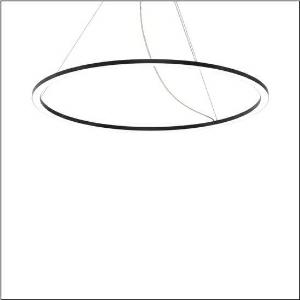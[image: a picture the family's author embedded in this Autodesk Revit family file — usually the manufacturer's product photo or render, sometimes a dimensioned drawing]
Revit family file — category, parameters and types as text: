
# Revit family: silica_r__21_ring-d_5pjbd4d1104a_1e9f
name_source: partatom
category: Lighting Fixtures
units: mm (PartAtom-declared; Revit-internal decimal feet)

## family parameters
Cut with Voids When Loaded = No
Host = Face
Light Source = No
Part Type = Normal
Room Calculation Point = No
Round Connector Dimension = Use Diameter
Shared = No

## types (1)
- Silica® 21 Ring-D (1 x LED, 10840 lm, 125 W, 3000K)
    Apparent Load = 125 VA
    CIE Flux Codes = 37 69 92 100 100
    Color Rendering = 80
    Color Temperature = 3000K
    Default Elevation = 1800 mm
    Description = Silica® 21 Ring-D, suspended luminaire, of PMMA, frosted, light emission: ring underside luminous distribution, primary light characteristic: symmetric, installation type: suspended mounting, LED, rated luminous flux: 10.840lm, luminous efficacy: 87lm/W, light colour: 830, colour temperature: 3000K, control gear: DALI 2, with terminal, 5-pole, mains connection: 230V, AC/DC, 0/50..60Hz, rated input power: 125W, housing, of extruded aluminium section, jet black (RAL 9005), diameter: 1.450mm, ceiling canopy, jet black (RAL 9005), protection rating (lamp compartment): IP40, insulation class (complete): insulation class I (protective earthing), certification: CE, impact resistance: IK02, permissible operating ambient temperature: 0..+35°C, packaging unit: 1 piece
    Height = 25 mm  [stored 0.082021 ft]
    Lamp = 1 x LED
    Lamp Light Flux = 10840 lm
    Lamp Power = 125 W
    Lamp count = 1
    Length = 1450 mm
    Luminous efficacy = 87 lm/W
    Manufacturer = Siteco
    ModVariant = No
    Model = 5PJBD4D1104A
    Mounting Place = Ceiling
    Mounting Type = Pendant
    Number of Poles = 1
    OnlyDefault = Yes
    Power Factor = 1
    Product Name = Silica® 21 Ring-D
    Product group = suspended luminaire
    ProductGroupID = 905
    Protection Class = Protection class I
    Protection Degree = IP 40
    RLX_Detail_Level = 1
    RLX_Emergency_Light_Flux = 0 lm
    RLX_Emergency_Type = 0
    RLX_Emergency_Type_DB = No
    RlxData = <blob elided: 19413 chars, md5=b3e99a7f>
    Socket = socket
    Standby Power = 0 W
    System Light Flux = 10840 lm
    System Power = 125 W
    Type Comments = Product without accessories
    Type Image = l_1258357.jpg
    URL = http://relux.com
    VarID = ---
    Voltage = 0 V
    Weight = 0.00 kg
    Width = 0 mm  [stored 0 ft]

note: [stored X ft] marks values corroborated as IEEE doubles in the binary element streams (Revit-internal decimal feet)

## geometry (parser evidence)
native form markers: Blend x4, Sweep x12
no freeform markers — native parametric forms only
